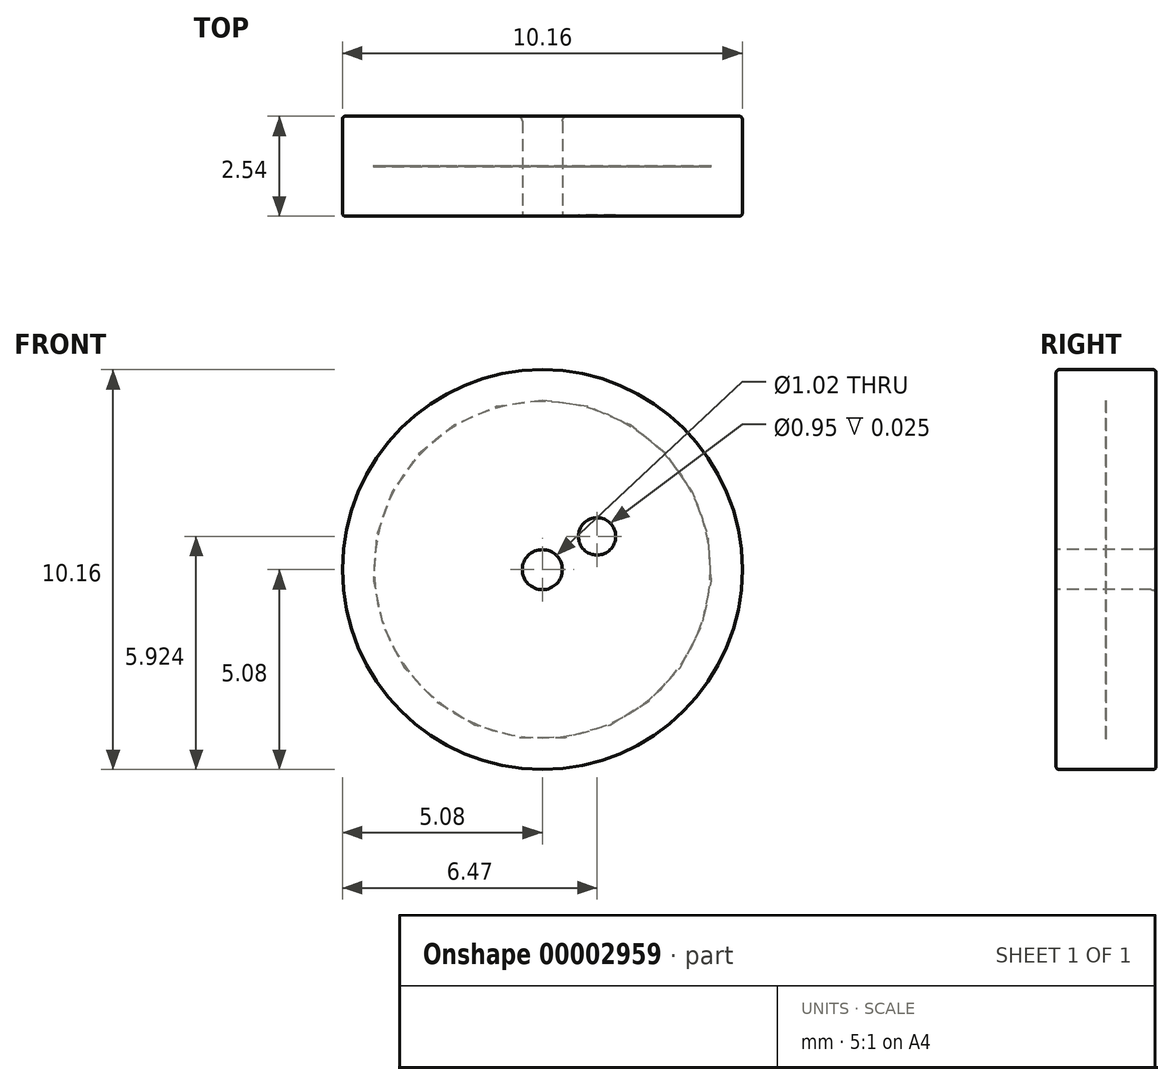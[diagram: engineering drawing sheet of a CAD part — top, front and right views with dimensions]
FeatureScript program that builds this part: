
annotation { "Feature Type Name" : "Feature", "Feature Type Description" : "" }
export const myFeature = defineFeature(function(context is Context, id is Id, definition is map)
    precondition{}
    {
        {
            var Q0;
            Q0=qCreatedBy(makeId("Front.planeOp"),FACE);
            var sketch = newSketch(context, id + "F0", { "sketchPlane" : qUnion([Q0])});
            skCircle(sketch, "E0", {"center": v(0, 0) * mm, "radius": 5.08 * mm});
            skSolve(sketch);
        }
        {
            var Q0;
            Q0=makeQuery(id+"F0.imprint","IMPRINT",FACE,{"disambiguationData":[TD([[makeQuery(id+"F0.imprint","IMPRINT",EDGE,{"derivedFrom":sQuery(id+"F0.wireOp",EDGE,"E0")}),1.0]])]});
            extrude(context, id + "F1", {"entities" : qUnion([Q0]), "depth" : 1.27 * mm});
        }
        {
            var Q0;
            Q0=makeQuery(id+"F1.opExtrude","SWEPT_BODY",BODY,{"disambiguationData":[OSD([sQuery(id+"F0.wireOp",EDGE,"E0")])]});
            var Q1;
            Q1=qCreatedBy(makeId("Front.planeOp"),FACE);
            mirror(context, id + "F2", {"entities" : qUnion([Q0]), "mirrorPlane" : qUnion([Q1])});
        }
        {
            var Q0;
            Q0=makeQuery(id+"F1.opExtrude","SWEPT_BODY",BODY,{"disambiguationData":[OSD([sQuery(id+"F0.wireOp",EDGE,"E0")])]});
            var Q1;
            Q1=makeQuery(id+"F2.opPattern","COPY",BODY,{"derivedFrom":makeQuery(id+"F1.opExtrude","SWEPT_BODY",BODY,{"disambiguationData":[OSD([sQuery(id+"F0.wireOp",EDGE,"E0")])]}),"instanceName":"1"});
            booleanBodies(context, id + "F3", {"operationType" : BooleanOperationType.UNION, "tools" : qUnion([Q0, Q1])});
        }
        {
            var Q0;
            Q0=qCreatedBy(makeId("Right.planeOp"),FACE);
            var sketch = newSketch(context, id + "F4", { "sketchPlane" : qUnion([Q0])});
            skFitSpline(sketch, "E1", {"points": [v(-0.93, 5.81) * mm, v(-0.73, 4.54) * mm, v(0, 4.27) * mm, v(0, 4.3) * mm], "startDerivative": vector(-0.19, -3.22) * mm, "endDerivative": vector(0, 0.54) * mm});
            skLineSegment(sketch, "E2", {"start": v(-0.93, 5.81) * mm, "end": v(0, 5.81) * mm});
            skLineSegment(sketch, "E3", {"start": v(0, 5.81) * mm, "end": v(0, 4.29) * mm, "construction": true});
            skLineSegment(sketch, "E4.0.MirrorCS", {"start": v(0.93, 5.81) * mm, "end": v(0, 5.81) * mm});
            skFitSpline(sketch, "E5.0.MirrorCS", {"points": [v(0.93, 5.81) * mm, v(0.73, 4.54) * mm, v(0, 4.27) * mm, v(0, 4.3) * mm], "startDerivative": vector(0.19, -3.22) * mm, "endDerivative": vector(0, 0.54) * mm});
            skLineSegment(sketch, "E6.trimOffspring", {"start": v(0, 4.3) * mm, "end": v(0, 4.3) * mm});
            skSolve(sketch);
        }
        {
            var Q0;
            Q0=makeQuery(id+"F4.imprint","IMPRINT",FACE,{"disambiguationData":[TD([[makeQuery(id+"F4.imprint","IMPRINT",EDGE,{"derivedFrom":sQuery(id+"F4.wireOp",EDGE,"E1")}),1.0]])]});
            var Q1;
            Q1=makeQuery(id+"F1.opExtrude","CAP_EDGE",EDGE,{"disambiguationData":[OSD([sQuery(id+"F0.wireOp",EDGE,"E0")])],"isStart":false});
            revolve(context, id + "F5", {"operationType" : NewBodyOperationType.REMOVE, "entities" : qUnion([Q0]), "axis" : qUnion([Q1]), "revolveType" : RevolveType.FULL, "oppositeDirection" : true});
        }
        {
            var Q0;
            Q0=makeQuery(id+"F1.opExtrude","CAP_FACE",FACE,{"disambiguationData":[OSD([sQuery(id+"F0.wireOp",EDGE,"E0")])],"isStart":false});
            var sketch = newSketch(context, id + "F6", { "sketchPlane" : qUnion([Q0])});
            skCircle(sketch, "E7", {"center": v(0, 0) * mm, "radius": 0.5 * mm});
            skSolve(sketch);
        }
        {
            var Q0;
            Q0=makeQuery(id+"F6.imprint","IMPRINT",FACE,{"disambiguationData":[TD([[makeQuery(id+"F6.imprint","IMPRINT",EDGE,{"derivedFrom":sQuery(id+"F6.wireOp",EDGE,"E7")}),1.0]])]});
            extrude(context, id + "F7", {"entities" : qUnion([Q0]), "operationType" : NewBodyOperationType.REMOVE, "endBound" : BoundingType.THROUGH_ALL, "oppositeDirection" : true, "depth" : 25.4 * mm});
        }
        {
            var Q0;
            Q0=makeQuery(id+"F1.opExtrude","CAP_EDGE",EDGE,{"disambiguationData":[OSD([sQuery(id+"F0.wireOp",EDGE,"E0")])],"isStart":false});
            var Q1;
            {var subQ0=makeQuery(id+"F1.opExtrude","SWEPT_FACE",FACE,{"disambiguationData":[OSD([sQuery(id+"F0.wireOp",EDGE,"E0")])]});Q1=makeQuery(id+"F5.boolean.opBoolean","INTERSECT",EDGE,{"derivedFrom":[makeQuery(id+"F3.opBoolean","MERGE",FACE,{"derivedFrom":[subQ0,makeQuery(id+"F2.opPattern","COPY",FACE,{"derivedFrom":subQ0,"instanceName":"1"})]}),makeQuery(id+"F5.opRevolve","SWEPT_FACE",FACE,{"disambiguationData":[OSD([sQuery(id+"F4.wireOp",EDGE,"E1")])]})]});}
            var Q2;
            {var subQ0=makeQuery(id+"F1.opExtrude","SWEPT_FACE",FACE,{"disambiguationData":[OSD([sQuery(id+"F0.wireOp",EDGE,"E0")])]});Q2=makeQuery(id+"F5.boolean.opBoolean","INTERSECT",EDGE,{"derivedFrom":[makeQuery(id+"F3.opBoolean","MERGE",FACE,{"derivedFrom":[subQ0,makeQuery(id+"F2.opPattern","COPY",FACE,{"derivedFrom":subQ0,"instanceName":"1"})]}),makeQuery(id+"F5.opRevolve","SWEPT_FACE",FACE,{"disambiguationData":[OSD([sQuery(id+"F4.wireOp",EDGE,"E5.0.MirrorCS")])]})]});}
            var Q3;
            Q3=makeQuery(id+"F2.opPattern","COPY",EDGE,{"derivedFrom":makeQuery(id+"F1.opExtrude","CAP_EDGE",EDGE,{"disambiguationData":[OSD([sQuery(id+"F0.wireOp",EDGE,"E0")])],"isStart":false}),"instanceName":"1"});
            fillet(context, id + "F8", {"entities" : qUnion([Q0, Q1, Q2, Q3]), "radius" : 0.08 * mm, "tangentPropagation" : true, "allowEdgeOverflow" : false});
        }
        {
            var Q0;
            Q0=makeQuery(id+"F7.boolean.opBoolean","COPY",EDGE,{"derivedFrom":makeQuery(id+"F7.opExtrude","CAP_EDGE",EDGE,{"disambiguationData":[OSD([sQuery(id+"F6.wireOp",EDGE,"E7")])],"isStart":true})});
            var Q1;
            Q1=makeQuery(id+"F7.boolean.opBoolean","INTERSECT",EDGE,{"derivedFrom":[makeQuery(id+"F2.opPattern","COPY",FACE,{"derivedFrom":makeQuery(id+"F1.opExtrude","CAP_FACE",FACE,{"disambiguationData":[OSD([sQuery(id+"F0.wireOp",EDGE,"E0")])],"isStart":false}),"instanceName":"1"}),makeQuery(id+"F7.opExtrude","SWEPT_FACE",FACE,{"disambiguationData":[OSD([sQuery(id+"F6.wireOp",EDGE,"E7")])]})]});
            fillet(context, id + "F9", {"entities" : qUnion([Q0, Q1]), "radius" : 0.13 * mm, "tangentPropagation" : true, "allowEdgeOverflow" : false});
        }
        {
            var Q0;
            Q0=makeQuery(id+"F6.imprint","IMPRINT",FACE,{"disambiguationData":[TD([[makeQuery(id+"F6.imprint","IMPRINT",EDGE,{"derivedFrom":sQuery(id+"F6.wireOp",EDGE,"E7")}),-1.0]])]});
            var sketch = newSketch(context, id + "F10", { "sketchPlane" : qUnion([Q0])});
            skCircle(sketch, "E8", {"center": v(1.39, 0.84) * mm, "radius": 0.47 * mm});
            skSolve(sketch);
        }
        {
            var Q0;
            Q0=makeQuery(id+"F10.imprint","IMPRINT",FACE,{"disambiguationData":[TD([[makeQuery(id+"F10.imprint","IMPRINT",EDGE,{"derivedFrom":sQuery(id+"F10.wireOp",EDGE,"E8")}),1.0]])]});
            extrude(context, id + "F11", {"entities" : qUnion([Q0]), "operationType" : NewBodyOperationType.REMOVE, "oppositeDirection" : true, "depth" : 0.03 * mm});
        }
    });
